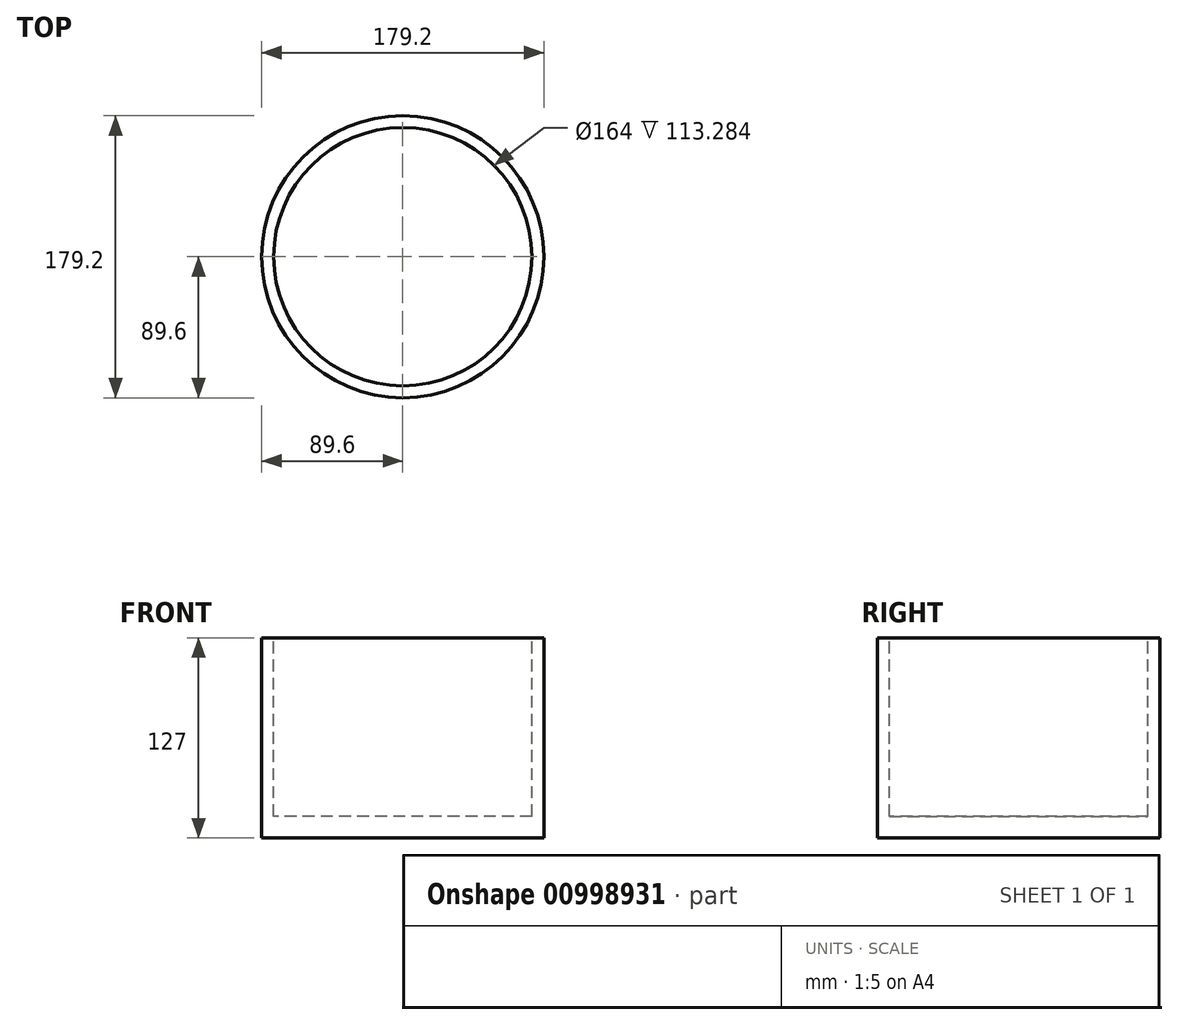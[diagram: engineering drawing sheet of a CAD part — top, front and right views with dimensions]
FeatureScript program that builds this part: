
annotation { "Feature Type Name" : "Feature", "Feature Type Description" : "" }
export const myFeature = defineFeature(function(context is Context, id is Id, definition is map)
    precondition{}
    {
        {
            var Q0;
            Q0=qCreatedBy(makeId("Front.planeOp"),FACE);
            var sketch = newSketch(context, id + "F0", { "sketchPlane" : qUnion([Q0])});
            skLineSegment(sketch, "E0.bottom", {"start": v(0, 0) * mm, "end": v(89.6, 0) * mm});
            skLineSegment(sketch, "E0.top", {"start": v(0, 127) * mm, "end": v(89.6, 127) * mm});
            skLineSegment(sketch, "E0.left", {"start": v(0, 0) * mm, "end": v(0, 127) * mm});
            skLineSegment(sketch, "E0.right", {"start": v(89.6, 0) * mm, "end": v(89.6, 127) * mm});
            skLineSegment(sketch, "E1.bottom", {"start": v(0, 0) * mm, "end": v(0, 0) * mm});
            skLineSegment(sketch, "E1.top", {"start": v(0, 237.34) * mm, "end": v(0, 237.34) * mm});
            skLineSegment(sketch, "E1.left", {"start": v(0, 0) * mm, "end": v(0, 237.34) * mm, "construction": true});
            skLineSegment(sketch, "E1.right", {"start": v(0, 0) * mm, "end": v(0, 237.34) * mm, "construction": true});
            skSolve(sketch);
        }
        {
            var Q0;
            Q0=makeQuery(id+"F0.imprint","IMPRINT",FACE,{"disambiguationData":[TD([[makeQuery(id+"F0.imprint","IMPRINT",EDGE,{"derivedFrom":sQuery(id+"F0.wireOp",EDGE,"E0.bottom")}),1.0]])]});
            var Q1;
            Q1=sQuery(id+"F0.wireOp",EDGE,"E1.right");
            revolve(context, id + "F1", {"surfaceOperationType" : NewSurfaceOperationType.NEW, "entities" : qUnion([Q0]), "axis" : qUnion([Q1]), "revolveType" : RevolveType.FULL});
        }
        {
            var Q0;
            Q0=makeQuery(id+"F1.opRevolve","SWEPT_FACE",FACE,{"disambiguationData":[OSD([sQuery(id+"F0.wireOp",EDGE,"E0.top")])]});
            var sketch = newSketch(context, id + "F2", { "sketchPlane" : qUnion([Q0])});
            skCircle(sketch, "E2", {"center": v(0, 0) * mm, "radius": 82 * mm});
            skSolve(sketch);
        }
        {
            var Q0;
            Q0=makeQuery(id+"F2.imprint","IMPRINT",FACE,{"disambiguationData":[TD([[makeQuery(id+"F2.imprint","IMPRINT",EDGE,{"derivedFrom":sQuery(id+"F2.wireOp",EDGE,"E2")}),1.0]])]});
            extrude(context, id + "F3", {"entities" : qUnion([Q0]), "operationType" : NewBodyOperationType.REMOVE, "oppositeDirection" : true, "depth" : 113.28 * mm, "offsetDistance" : 25.4 * mm});
        }
    });
